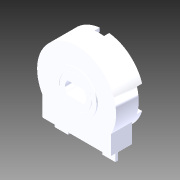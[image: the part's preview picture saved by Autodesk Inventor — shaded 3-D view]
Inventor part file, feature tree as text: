
AUTODESK INVENTOR PART (.ipt)
format: ipt  version: 2013 (Build 170138000, 138)  size: 187,392 bytes
history: native  units: in
note: dims shown in document units (in); Inventor stores cm internally (conversion verified against a paired STEP export)
features: extrude x7, sketch x5, mirror x1
ambient origin geometry x8: Origin, YZ Plane, XZ Plane, XY Plane, X Axis, Y Axis, Z Axis, Center Point
bodies: Solid1 (feature_tree)
feature tree (13):
  sketch  "Sketch1"  dims[d0=0.169in d1=0.0in d2=0.039in d3=0.0in]
  extrude  "Extrusion1"  Depth=0.039in TaperAngle=0.0deg
  sketch  "Sketch2"  dims[d4=0.039in d5=0.0in d6=0.008in d7=0.0in]
  extrude  "Extrusion2"  Depth=0.008in TaperAngle=0.0deg
  extrude  "Extrusion3"  Depth=0.012in TaperAngle=0.0deg
  extrude  "Extrusion4"  Depth=0.079in TaperAngle=0.0deg
  extrude  "Extrusion5"  [1 undecoded]
  mirror  "Mirror1"
  sketch  "Sketch4"  dims[d11=0.079in d12=0.0in d13=0.079in d14=0.0in]
  extrude  "Extrusion6"  [1 undecoded]
  extrude  "Extrusion7"  [1 undecoded]
  sketch  "Sketch3"  dims[d8=0.008in d9=0.012in d10=0.0in]
  sketch  "Sketch5"
note: 3 required parameter values undecoded (feature->parameter linkage not recoverable at this tier; creation-order binding heuristic only, values carry confidence <= 0.55)
